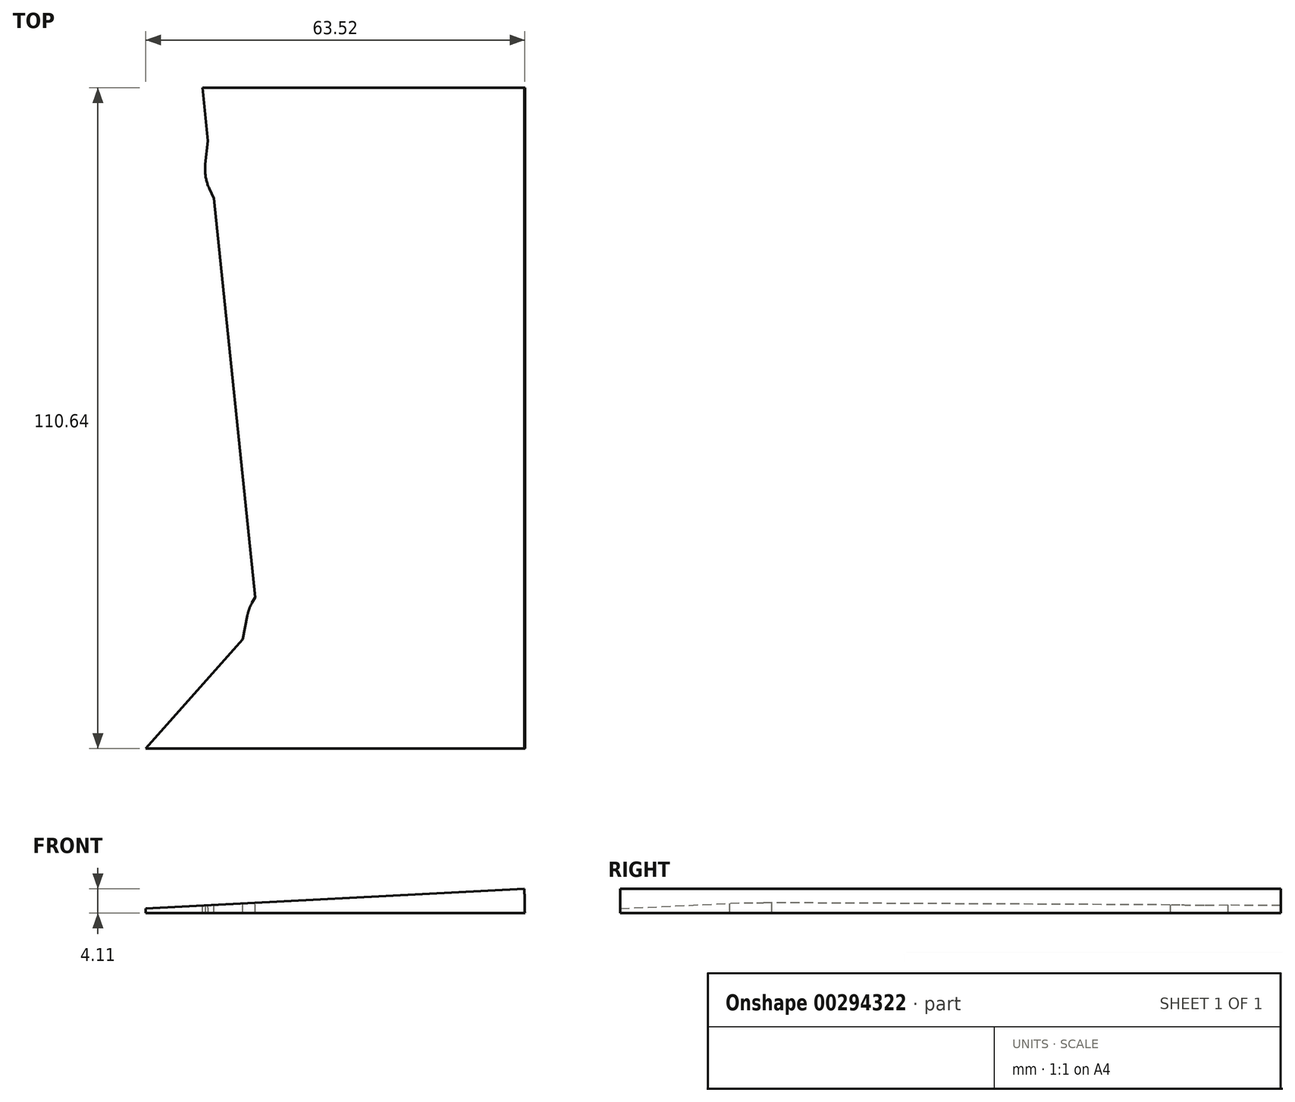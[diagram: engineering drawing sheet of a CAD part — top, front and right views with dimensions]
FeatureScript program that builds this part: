
annotation { "Feature Type Name" : "Feature", "Feature Type Description" : "" }
export const myFeature = defineFeature(function(context is Context, id is Id, definition is map)
    precondition{}
    {
        {
            var Q0;
            Q0=qCreatedBy(makeId("Top.planeOp"),FACE);
            var sketch = newSketch(context, id + "F0", { "sketchPlane" : qUnion([Q0])});
            skPoint(sketch, "E0.visualSharp", {"position": v(33.77, 14.05) * mm});
            skLineSegment(sketch, "E1", {"start": v(24.5, 110.64) * mm, "end": v(78.48, 110.64) * mm});
            skLineSegment(sketch, "E2", {"start": v(78.48, 110.64) * mm, "end": v(78.48, 0) * mm});
            skLineSegment(sketch, "E3", {"start": v(78.48, 0) * mm, "end": v(14.98, 0) * mm});
            skPoint(sketch, "E4.end.orphan", {"position": v(-11.84, 110.64) * mm});
            skPoint(sketch, "E5.visualSharp", {"position": v(33.77, 21.15) * mm});
            skPoint(sketch, "E6.centerSnap0", {"position": v(32.66, 21.51) * mm});
            skPoint(sketch, "E6.center.orphan", {"position": v(32.66, 21.15) * mm});
            skLineSegment(sketch, "E7", {"start": v(24.5, 110.64) * mm, "end": v(25.41, 101.78) * mm});
            skLineSegment(sketch, "E8", {"start": v(14.98, 0) * mm, "end": v(31.23, 18.3) * mm});
            skLineSegment(sketch, "E9", {"start": v(33.33, 25.34) * mm, "end": v(32.8, 24.34) * mm});
            skLineSegment(sketch, "E10", {"start": v(32.03, 22.22) * mm, "end": v(31.23, 18.3) * mm});
            skPoint(sketch, "E11.visualSharp", {"position": v(32.25, 23.34) * mm});
            skArc(sketch, "E11.filletArc", {"start": v(32.8, 24.34) * mm, "mid": v(32.33, 23.31) * mm, "end": v(32.03, 22.22) * mm});
            skLineSegment(sketch, "E12", {"start": v(25.41, 101.78) * mm, "end": v(24.98, 97.83) * mm});
            skLineSegment(sketch, "E13", {"start": v(25.64, 93.8) * mm, "end": v(26.42, 92.11) * mm});
            skLineSegment(sketch, "E14.trimOffspring", {"start": v(26.42, 92.11) * mm, "end": v(33.33, 25.34) * mm});
            skPoint(sketch, "E15.visualSharp", {"position": v(24.75, 95.72) * mm});
            skArc(sketch, "E15.filletArc", {"start": v(24.98, 97.83) * mm, "mid": v(25.03, 95.77) * mm, "end": v(25.64, 93.8) * mm});
            skSolve(sketch);
        }
        {
            var Q0;
            Q0=qCreatedBy(makeId("Top.planeOp"),FACE);
            var sketch = newSketch(context, id + "F1", { "sketchPlane" : qUnion([Q0])});
            skLineSegment(sketch, "E16", {"start": v(0, 0) * mm, "end": v(0, 82.54) * mm});
            skSolve(sketch);
        }
        {
            var Q0;
            Q0=makeQuery(id+"F0.imprint","IMPRINT",FACE,{"disambiguationData":[TD([[makeQuery(id+"F0.imprint","IMPRINT",EDGE,{"derivedFrom":sQuery(id+"F0.wireOp",EDGE,"E1")}),-1.0]])]});
            var Q1;
            Q1=sQuery(id+"F1.wireOp",EDGE,"E16");
            revolve(context, id + "F2", {"entities" : qUnion([Q0]), "axis" : qUnion([Q1]), "revolveType" : RevolveType.ONE_DIRECTION, "oppositeDirection" : true, "angle" : 3 * degree});
        }
    });
